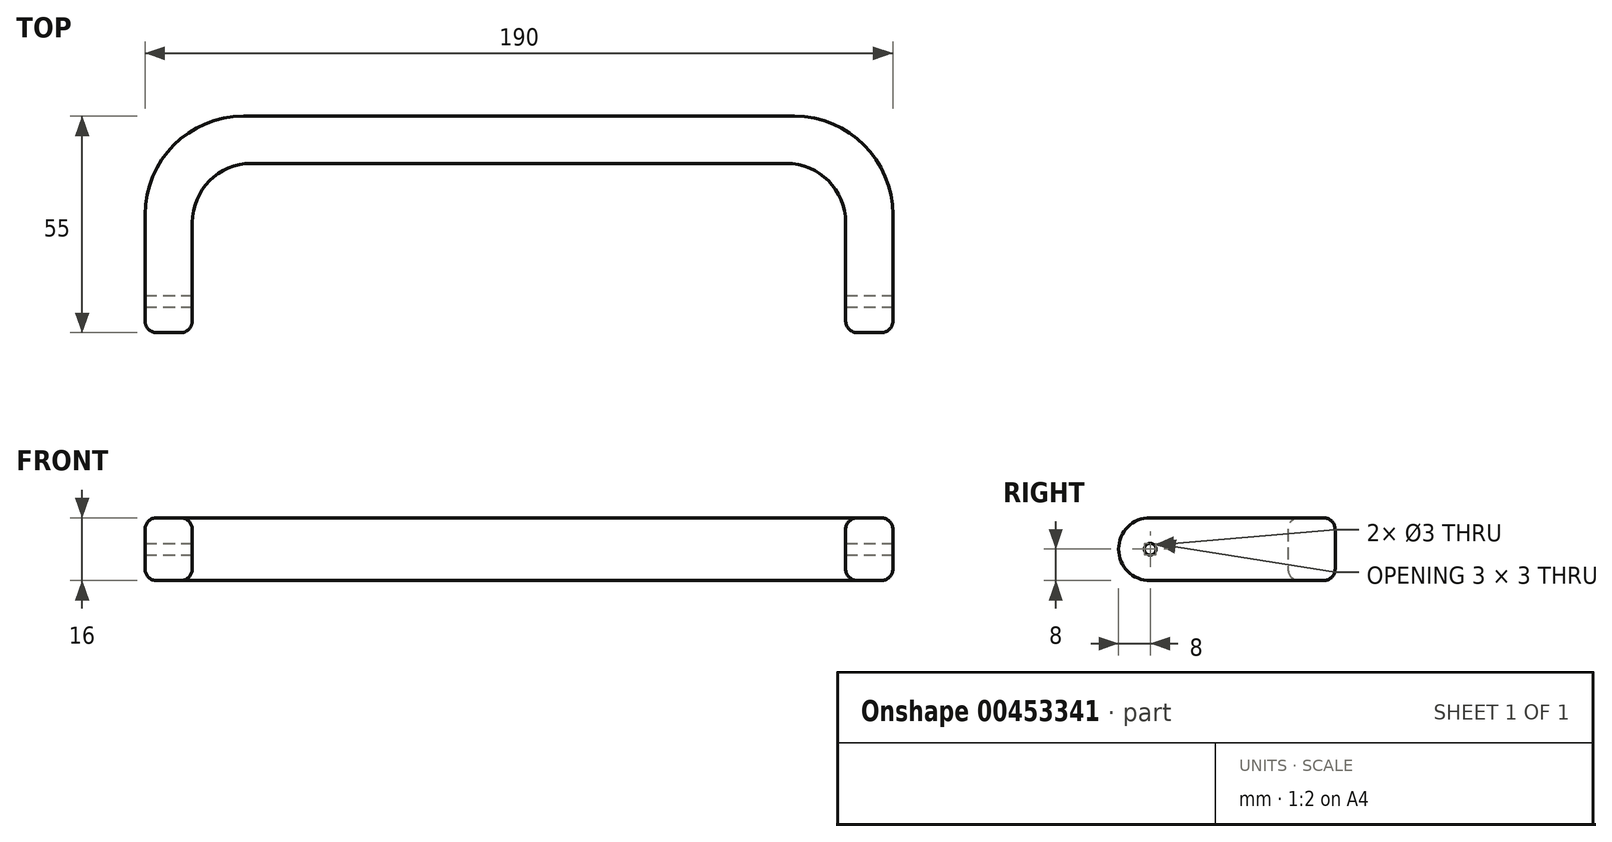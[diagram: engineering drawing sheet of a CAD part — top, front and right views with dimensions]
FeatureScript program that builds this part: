
annotation { "Feature Type Name" : "Feature", "Feature Type Description" : "" }
export const myFeature = defineFeature(function(context is Context, id is Id, definition is map)
    precondition{}
    {
        {
            var Q0;
            Q0=qCreatedBy(makeId("Top.planeOp"),FACE);
            var sketch = newSketch(context, id + "F0", { "sketchPlane" : qUnion([Q0])});
            skLineSegment(sketch, "E0", {"start": v(0, 35.78) * mm, "end": v(-95, 35.78) * mm});
            skLineSegment(sketch, "E1", {"start": v(-95, 35.78) * mm, "end": v(-95, -19.22) * mm});
            skLineSegment(sketch, "E2", {"start": v(-95, -19.22) * mm, "end": v(-83, -19.22) * mm});
            skLineSegment(sketch, "E3", {"start": v(-83, -19.22) * mm, "end": v(-83, 23.78) * mm});
            skLineSegment(sketch, "E4", {"start": v(-83, 23.78) * mm, "end": v(0, 23.78) * mm});
            skLineSegment(sketch, "E5.MirrorCS", {"start": v(0, 35.78) * mm, "end": v(95, 35.78) * mm});
            skLineSegment(sketch, "E6.MirrorCS", {"start": v(83, 23.78) * mm, "end": v(0, 23.78) * mm});
            skLineSegment(sketch, "E7.MirrorCS", {"start": v(83, -19.22) * mm, "end": v(83, 23.78) * mm});
            skLineSegment(sketch, "E8.MirrorCS", {"start": v(95, 35.78) * mm, "end": v(95, -19.22) * mm});
            skLineSegment(sketch, "E9.MirrorCS", {"start": v(95, -19.22) * mm, "end": v(83, -19.22) * mm});
            skSolve(sketch);
        }
        {
            var Q0;
            Q0 = qSketchRegion(id + "F0", true);
            extrude(context, id + "F1", {"entities" : qUnion([Q0]), "depth" : 16 * mm});
        }
        {
            var Q0;
            Q0=makeQuery(id+"F1.opExtrude","SWEPT_EDGE",EDGE,{"disambiguationData":[OSD([sQuery(id+"F0.wireOp",EDGE,"E3"),sQuery(id+"F0.wireOp",EDGE,"E4")])]});
            var Q1;
            Q1=makeQuery(id+"F1.opExtrude","SWEPT_EDGE",EDGE,{"disambiguationData":[OSD([sQuery(id+"F0.wireOp",EDGE,"E6.MirrorCS"),sQuery(id+"F0.wireOp",EDGE,"E7.MirrorCS")])]});
            fillet(context, id + "F2", {"entities" : qUnion([Q0, Q1]), "radius" : 15 * mm, "tangentPropagation" : true, "allowEdgeOverflow" : false});
        }
        {
            var Q0;
            Q0=makeQuery(id+"F1.opExtrude","SWEPT_EDGE",EDGE,{"disambiguationData":[OSD([sQuery(id+"F0.wireOp",EDGE,"E0"),sQuery(id+"F0.wireOp",EDGE,"E1")])]});
            var Q1;
            Q1=makeQuery(id+"F1.opExtrude","SWEPT_EDGE",EDGE,{"disambiguationData":[OSD([sQuery(id+"F0.wireOp",EDGE,"E5.MirrorCS"),sQuery(id+"F0.wireOp",EDGE,"E8.MirrorCS")])]});
            fillet(context, id + "F3", {"entities" : qUnion([Q0, Q1]), "radius" : 25 * mm, "tangentPropagation" : true, "allowEdgeOverflow" : false});
        }
        {
            var Q0;
            Q0=makeQuery(id+"F1.opExtrude","CAP_EDGE",EDGE,{"disambiguationData":[OSD([sQuery(id+"F0.wireOp",EDGE,"E2")])],"isStart":false});
            var Q1;
            Q1=makeQuery(id+"F1.opExtrude","CAP_EDGE",EDGE,{"disambiguationData":[OSD([sQuery(id+"F0.wireOp",EDGE,"E2")])],"isStart":true});
            var Q2;
            Q2=makeQuery(id+"F1.opExtrude","CAP_EDGE",EDGE,{"disambiguationData":[OSD([sQuery(id+"F0.wireOp",EDGE,"E9.MirrorCS")])],"isStart":false});
            var Q3;
            Q3=makeQuery(id+"F1.opExtrude","CAP_EDGE",EDGE,{"disambiguationData":[OSD([sQuery(id+"F0.wireOp",EDGE,"E9.MirrorCS")])],"isStart":true});
            fillet(context, id + "F4", {"entities" : qUnion([Q0, Q1, Q2, Q3]), "radius" : 8 * mm, "tangentPropagation" : true, "allowEdgeOverflow" : false});
        }
        {
            var Q0;
            Q0=makeQuery(id+"F1.opExtrude","SWEPT_FACE",FACE,{"disambiguationData":[OSD([sQuery(id+"F0.wireOp",EDGE,"E8.MirrorCS")])]});
            var sketch = newSketch(context, id + "F5", { "sketchPlane" : qUnion([Q0])});
            skLineSegment(sketch, "E10", {"start": v(-11.22, 16) * mm, "end": v(-11.22, -0.95) * mm, "construction": true});
            skCircle(sketch, "E11", {"center": v(-11.22, 8) * mm, "radius": 1.5 * mm});
            skSolve(sketch);
        }
        {
            var Q0;
            Q0 = qSketchRegion(id + "F5", true);
            extrude(context, id + "F6", {"entities" : qUnion([Q0]), "operationType" : NewBodyOperationType.REMOVE, "oppositeDirection" : true, "depth" : 250 * mm});
        }
        {
            var Q0;
            Q0=makeQuery(id+"F1.opExtrude","CAP_FACE",FACE,{"disambiguationData":[OSD([sQuery(id+"F0.wireOp",EDGE,"E0"),sQuery(id+"F0.wireOp",EDGE,"E1"),sQuery(id+"F0.wireOp",EDGE,"E2"),sQuery(id+"F0.wireOp",EDGE,"E3"),sQuery(id+"F0.wireOp",EDGE,"E4"),sQuery(id+"F0.wireOp",EDGE,"E5.MirrorCS"),sQuery(id+"F0.wireOp",EDGE,"E6.MirrorCS"),sQuery(id+"F0.wireOp",EDGE,"E7.MirrorCS"),sQuery(id+"F0.wireOp",EDGE,"E8.MirrorCS"),sQuery(id+"F0.wireOp",EDGE,"E9.MirrorCS")])],"isStart":true});
            fillet(context, id + "F7", {"entities" : qUnion([Q0]), "radius" : 3 * mm, "tangentPropagation" : true, "allowEdgeOverflow" : false});
        }
    });
